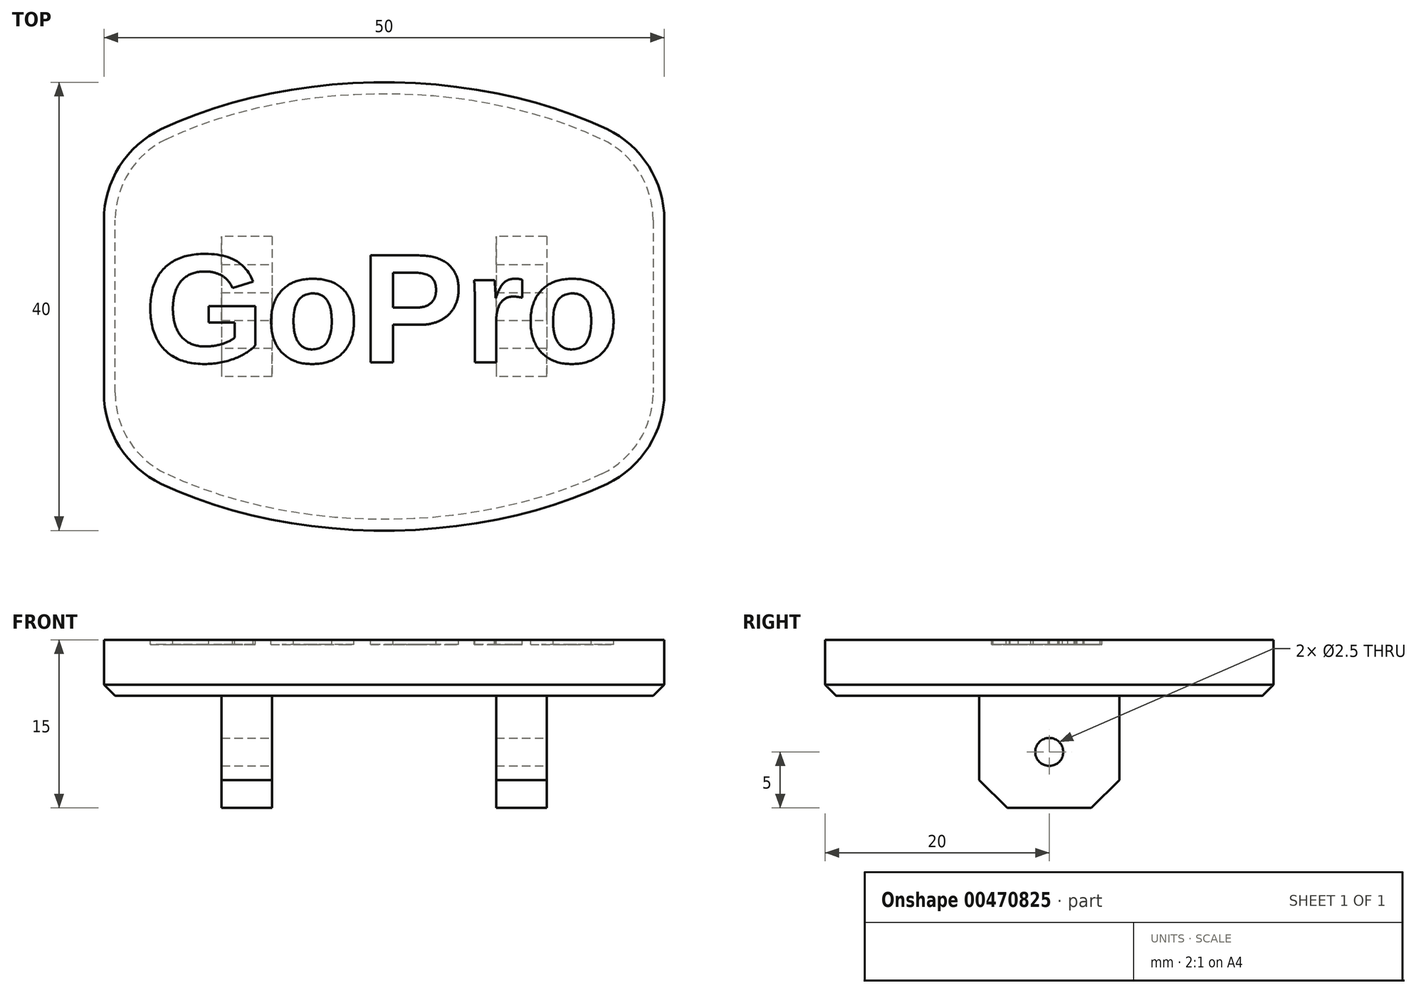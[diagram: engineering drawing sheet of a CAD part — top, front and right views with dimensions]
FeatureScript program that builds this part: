
annotation { "Feature Type Name" : "Feature", "Feature Type Description" : "" }
export const myFeature = defineFeature(function(context is Context, id is Id, definition is map)
    precondition{}
    {
        {
            var Q0;
            Q0=qCreatedBy(makeId("Top.planeOp"),FACE);
            var sketch = newSketch(context, id + "F0", { "sketchPlane" : qUnion([Q0])});
            skLineSegment(sketch, "E0.left", {"start": v(25, -7.7) * mm, "end": v(25, 7.7) * mm});
            skLineSegment(sketch, "E0.right", {"start": v(-25, -7.7) * mm, "end": v(-25, 7.7) * mm});
            skPoint(sketch, "E0.middle", {"position": v(0, 0) * mm});
            skEllipticalArc(sketch, "E1", {});
            skPoint(sketch, "E2.visualSharp", {"position": v(-25, 12.78) * mm});
            skArc(sketch, "E2.filletArc", {"start": v(-19.86, 15.83) * mm, "mid": v(-23.6, 12.5) * mm, "end": v(-25, 7.7) * mm});
            skArc(sketch, "E3.filletArc", {"start": v(-25, -7.7) * mm, "mid": v(-23.6, -12.5) * mm, "end": v(-19.86, -15.83) * mm});
            skEllipticalArc(sketch, "E4.trimOffspring", {});
            skPoint(sketch, "E5.visualSharp", {"position": v(25, 12.78) * mm});
            skArc(sketch, "E5.filletArc", {"start": v(25, 7.7) * mm, "mid": v(23.6, 12.5) * mm, "end": v(19.86, 15.83) * mm});
            skPoint(sketch, "E6.visualSharp", {"position": v(25, -12.78) * mm});
            skArc(sketch, "E6.filletArc", {"start": v(19.86, -15.83) * mm, "mid": v(23.6, -12.5) * mm, "end": v(25, -7.7) * mm});
            const initialGuessF0  = {"E1": [0, 0, 1, 0, 0.0325, 0.02, 4.054867696901255, 5.3699102638681255], "E4.trimOffspring": [0, 0, 1, 0, 0.0325, 0.02, 0.913275043311461, 2.2283176102783337]};
            skSetInitialGuess(sketch, initialGuessF0);
            skSolve(sketch);
        }
        {
            var Q0;
            Q0=makeQuery(id+"F0.imprint","IMPRINT",FACE,{"disambiguationData":[TD([[makeQuery(id+"F0.imprint","IMPRINT",EDGE,{"derivedFrom":sQuery(id+"F0.wireOp",EDGE,"E0.left")}),1.0]])]});
            extrude(context, id + "F1", {"entities" : qUnion([Q0]), "depth" : 5 * mm});
        }
        {
            var Q0;
            Q0=makeQuery(id+"F1.opExtrude","CAP_FACE",FACE,{"disambiguationData":[OSD([sQuery(id+"F0.wireOp",EDGE,"E0.left"),sQuery(id+"F0.wireOp",EDGE,"E0.right"),sQuery(id+"F0.wireOp",EDGE,"E1"),sQuery(id+"F0.wireOp",EDGE,"E2.filletArc"),sQuery(id+"F0.wireOp",EDGE,"E3.filletArc"),sQuery(id+"F0.wireOp",EDGE,"E4.trimOffspring"),sQuery(id+"F0.wireOp",EDGE,"E5.filletArc"),sQuery(id+"F0.wireOp",EDGE,"E6.filletArc")])],"isStart":true});
            var sketch = newSketch(context, id + "F2", { "sketchPlane" : qUnion([Q0])});
            skLineSegment(sketch, "E7.bottom", {"start": v(14.5, -6.25) * mm, "end": v(10, -6.25) * mm});
            skLineSegment(sketch, "E7.top", {"start": v(14.5, 6.25) * mm, "end": v(10, 6.25) * mm});
            skLineSegment(sketch, "E7.left", {"start": v(14.5, -6.25) * mm, "end": v(14.5, 6.25) * mm});
            skLineSegment(sketch, "E7.right", {"start": v(-14.5, -6.25) * mm, "end": v(-14.5, 6.25) * mm});
            skPoint(sketch, "E7.middle", {"position": v(0, 0) * mm});
            skLineSegment(sketch, "E8.left", {"start": v(10, -6.25) * mm, "end": v(10, 6.25) * mm});
            skLineSegment(sketch, "E8.right", {"start": v(-10, -6.25) * mm, "end": v(-10, 6.25) * mm});
            skLineSegment(sketch, "E9.trimOffspring", {"start": v(-10, 6.25) * mm, "end": v(-14.5, 6.25) * mm});
            skLineSegment(sketch, "E10.trimOffspring", {"start": v(-10, -6.25) * mm, "end": v(-14.5, -6.25) * mm});
            skSolve(sketch);
        }
        {
            var Q0;
            Q0=makeQuery(id+"F1.opExtrude","CAP_EDGE",EDGE,{"disambiguationData":[OSD([sQuery(id+"F0.wireOp",EDGE,"E1")])],"isStart":true});
            var Q1;
            Q1=makeQuery(id+"FL3o96M6EoHQmEN_1.opExtrude","CAP_FACE",FACE,{"disambiguationData":[OSD([sQuery(id+"F2.wireOp",EDGE,"E7.bottom"),sQuery(id+"F2.wireOp",EDGE,"E7.top"),sQuery(id+"F2.wireOp",EDGE,"E7.left"),sQuery(id+"F2.wireOp",EDGE,"E7.right")])],"isStart":false});
            chamfer(context, id + "F3", {"entities" : qUnion([Q0, Q1]), "width" : 1 * mm, "tangentPropagation" : true});
        }
        {
            var Q0;
            Q0=makeQuery(id+"F1.opExtrude","CAP_FACE",FACE,{"disambiguationData":[OSD([sQuery(id+"F0.wireOp",EDGE,"E0.left"),sQuery(id+"F0.wireOp",EDGE,"E0.right"),sQuery(id+"F0.wireOp",EDGE,"E1"),sQuery(id+"F0.wireOp",EDGE,"E2.filletArc"),sQuery(id+"F0.wireOp",EDGE,"E3.filletArc"),sQuery(id+"F0.wireOp",EDGE,"E4.trimOffspring"),sQuery(id+"F0.wireOp",EDGE,"E5.filletArc"),sQuery(id+"F0.wireOp",EDGE,"E6.filletArc")])],"isStart":false});
            var sketch = newSketch(context, id + "F4", { "sketchPlane" : qUnion([Q0])});
            skText(sketch, "E11", { "text": "GoPro", "fontName": "Arimo-Bold.ttf"});
            const initialGuessF4  = {"E11": [-0.02143, -0.005, 1, 0, 0.01]};
            skSetInitialGuess(sketch, initialGuessF4);
            skSolve(sketch);
        }
        {
            var Q0;
            Q0=makeQuery(id+"F4.imprint","IMPRINT",FACE,{"disambiguationData":[TD([[makeQuery(id+"F4.imprint","IMPRINT",EDGE,{"derivedFrom":sQuery(id+"F4.wireOp",EDGE,"E11.sketch_text.stroke-0")}),-1.0]])]});
            var Q1;
            Q1=makeQuery(id+"F4.imprint","IMPRINT",FACE,{"disambiguationData":[TD([[makeQuery(id+"F4.imprint","IMPRINT",EDGE,{"derivedFrom":sQuery(id+"F4.wireOp",EDGE,"E11.sketch_text.stroke-21")}),-1.0]])]});
            var Q2;
            Q2=makeQuery(id+"F4.imprint","IMPRINT",FACE,{"disambiguationData":[TD([[makeQuery(id+"F4.imprint","IMPRINT",EDGE,{"derivedFrom":sQuery(id+"F4.wireOp",EDGE,"E11.sketch_text.stroke-35")}),-1.0]])]});
            var Q3;
            Q3=makeQuery(id+"F4.imprint","IMPRINT",FACE,{"disambiguationData":[TD([[makeQuery(id+"F4.imprint","IMPRINT",EDGE,{"derivedFrom":sQuery(id+"F4.wireOp",EDGE,"E11.sketch_text.stroke-51")}),-1.0]])]});
            var Q4;
            Q4=makeQuery(id+"F4.imprint","IMPRINT",FACE,{"disambiguationData":[TD([[makeQuery(id+"F4.imprint","IMPRINT",EDGE,{"derivedFrom":sQuery(id+"F4.wireOp",EDGE,"E11.sketch_text.stroke-68")}),-1.0]])]});
            extrude(context, id + "F5", {"entities" : qUnion([Q0, Q1, Q2, Q3, Q4]), "operationType" : NewBodyOperationType.REMOVE, "oppositeDirection" : true, "depth" : .4 * mm});
        }
        {
            var Q0;
            Q0=qSketchRegion(id+"F2",true);
            extrude(context, id + "F6", {"entities" : qUnion([Q0]), "operationType" : NewBodyOperationType.ADD, "depth" : 10 * mm});
        }
        {
            var Q0;
            Q0=makeQuery(id+"F6.opExtrude","CAP_EDGE",EDGE,{"disambiguationData":[OSD([sQuery(id+"F2.wireOp",EDGE,"E9.trimOffspring")])],"isStart":false});
            var Q1;
            Q1=makeQuery(id+"F6.opExtrude","CAP_EDGE",EDGE,{"disambiguationData":[OSD([sQuery(id+"F2.wireOp",EDGE,"E7.top")])],"isStart":false});
            var Q2;
            Q2=makeQuery(id+"F6.opExtrude","CAP_EDGE",EDGE,{"disambiguationData":[OSD([sQuery(id+"F2.wireOp",EDGE,"E10.trimOffspring")])],"isStart":false});
            var Q3;
            Q3=makeQuery(id+"F6.opExtrude","CAP_EDGE",EDGE,{"disambiguationData":[OSD([sQuery(id+"F2.wireOp",EDGE,"E7.bottom")])],"isStart":false});
            chamfer(context, id + "F7", {"entities" : qUnion([Q0, Q1, Q2, Q3]), "width" : 2.5 * mm, "tangentPropagation" : true});
        }
        {
            var Q0;
            Q0=makeQuery(id+"F6.opExtrude","SWEPT_FACE",FACE,{"disambiguationData":[OSD([sQuery(id+"F2.wireOp",EDGE,"E7.left")])]});
            var sketch = newSketch(context, id + "F8", { "sketchPlane" : qUnion([Q0])});
            skCircle(sketch, "E12", {"center": v(0, -5) * mm, "radius": 1.25 * mm});
            skSolve(sketch);
        }
        {
            var Q0;
            Q0=qSketchRegion(id+"F8",true);
            extrude(context, id + "F9", {"entities" : qUnion([Q0]), "operationType" : NewBodyOperationType.REMOVE, "endBound" : BoundingType.THROUGH_ALL, "oppositeDirection" : true, "depth" : 25 * mm});
        }
    });
